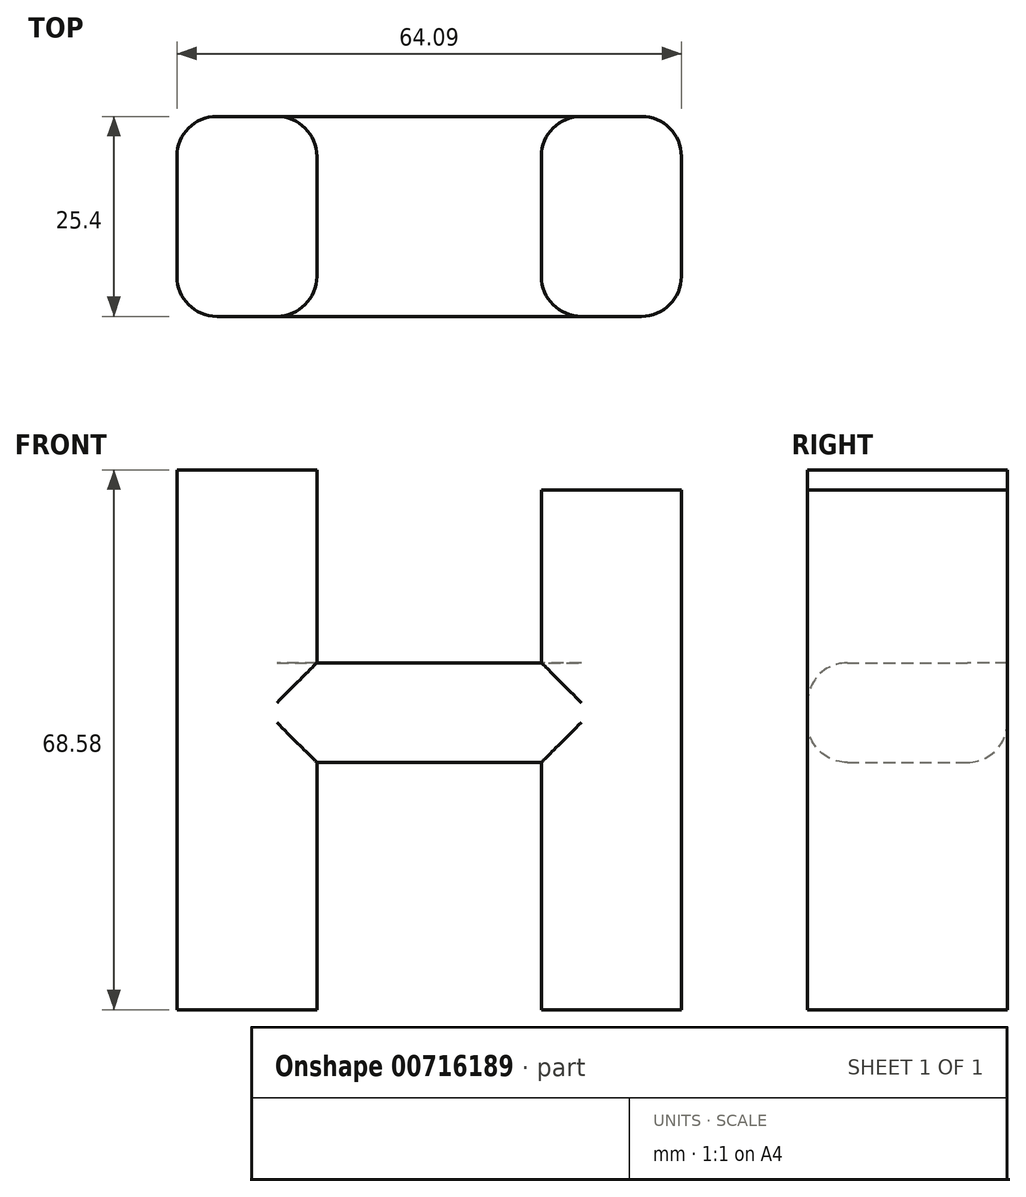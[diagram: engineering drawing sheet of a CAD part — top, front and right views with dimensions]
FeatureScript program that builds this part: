
annotation { "Feature Type Name" : "Feature", "Feature Type Description" : "" }
export const myFeature = defineFeature(function(context is Context, id is Id, definition is map)
    precondition{}
    {
        {
            var Q0;
            Q0=qCreatedBy(makeId("Front.planeOp"),FACE);
            var sketch = newSketch(context, id + "F0", { "sketchPlane" : qUnion([Q0])});
            skLineSegment(sketch, "E0.bottom", {"start": v(-8.9, 33.02) * mm, "end": v(8.9, 33.02) * mm});
            skLineSegment(sketch, "E0.top", {"start": v(-8.9, -33.02) * mm, "end": v(8.9, -33.02) * mm});
            skLineSegment(sketch, "E0.left", {"start": v(-8.9, 33.02) * mm, "end": v(-8.9, -33.02) * mm});
            skLineSegment(sketch, "E0.right", {"start": v(8.9, 33.02) * mm, "end": v(8.9, -33.02) * mm});
            skPoint(sketch, "E0.middle", {"position": v(0, 0) * mm});
            skLineSegment(sketch, "E1.bottom", {"start": v(37.42, 30.48) * mm, "end": v(55.2, 30.48) * mm});
            skLineSegment(sketch, "E1.top", {"start": v(37.42, -35.56) * mm, "end": v(55.2, -35.56) * mm});
            skLineSegment(sketch, "E1.left", {"start": v(37.42, 30.48) * mm, "end": v(37.42, -35.56) * mm});
            skLineSegment(sketch, "E1.right", {"start": v(55.2, 30.48) * mm, "end": v(55.2, -35.56) * mm});
            skLineSegment(sketch, "E2.bottom", {"start": v(8.9, 8.5) * mm, "end": v(37.42, 8.5) * mm});
            skLineSegment(sketch, "E2.top", {"start": v(8.9, -4.15) * mm, "end": v(37.42, -4.15) * mm});
            skLineSegment(sketch, "E2.left", {"start": v(8.9, 8.5) * mm, "end": v(8.9, -4.15) * mm});
            skLineSegment(sketch, "E2.right", {"start": v(37.42, 8.5) * mm, "end": v(37.42, -4.15) * mm});
            skLineSegment(sketch, "E3.top", {"start": v(-8.9, -35.56) * mm, "end": v(8.9, -35.56) * mm});
            skLineSegment(sketch, "E3.left", {"start": v(-8.9, -33.02) * mm, "end": v(-8.9, -35.56) * mm});
            skLineSegment(sketch, "E3.right", {"start": v(8.9, -33.02) * mm, "end": v(8.9, -35.56) * mm});
            skLineSegment(sketch, "E4.top", {"start": v(37.42, -31.16) * mm, "end": v(55.2, -31.16) * mm});
            skLineSegment(sketch, "E4.left", {"start": v(37.42, -31.16) * mm, "end": v(37.42, -35.56) * mm});
            skLineSegment(sketch, "E4.right", {"start": v(55.2, -31.16) * mm, "end": v(55.2, -35.56) * mm});
            skSolve(sketch);
        }
        {
            var Q0;
            {var subQ3=sQuery(id+"F0.wireOp",EDGE,"E0.bottom");Q0=makeQuery(id+"F0.imprint","IMPRINT",FACE,{"disambiguationData":[TD([[makeQuery(id+"F0.imprint","IMPRINT",EDGE,{"derivedFrom":subQ3}),-1.0]])]});}
            extrude(context, id + "F1", {"entities" : qUnion([Q0]), "depth" : 12.7 * mm, "offsetDistance" : 25.4 * mm});
        }
        {
            var Q0;
            Q0 = qSketchRegion(id + "F0", true);
            extrude(context, id + "F2", {"entities" : qUnion([Q0]), "operationType" : NewBodyOperationType.ADD, "depth" : 25.4 * mm, "offsetDistance" : 25.4 * mm});
        }
        {
            var Q0;
            Q0=makeQuery(id+"F2.opExtrude","CAP_EDGE",EDGE,{"disambiguationData":[OSD([sQuery(id+"F0.wireOp",EDGE,"E1.right"),sQuery(id+"F0.wireOp",EDGE,"E4.right")])],"isStart":false});
            var Q1;
            Q1=makeQuery(id+"F2.opExtrude","CAP_EDGE",EDGE,{"disambiguationData":[OSD([sQuery(id+"F0.wireOp",EDGE,"E1.right"),sQuery(id+"F0.wireOp",EDGE,"E4.right")])],"isStart":true});
            var Q2;
            Q2=makeQuery(id+"F2.opExtrude","CAP_EDGE",EDGE,{"disambiguationData":[OSD([sQuery(id+"F0.wireOp",EDGE,"E1.left")])],"isStart":false});
            var Q3;
            Q3=makeQuery(id+"F2.opExtrude","CAP_EDGE",EDGE,{"disambiguationData":[OSD([sQuery(id+"F0.wireOp",EDGE,"E0.right")])],"isStart":false});
            var Q4;
            Q4=makeQuery(id+"F2.opExtrude","CAP_EDGE",EDGE,{"disambiguationData":[OSD([sQuery(id+"F0.wireOp",EDGE,"E0.right"),sQuery(id+"F0.wireOp",EDGE,"E3.right")])],"isStart":false});
            var Q5;
            Q5=makeQuery(id+"F2.opExtrude","CAP_EDGE",EDGE,{"disambiguationData":[OSD([sQuery(id+"F0.wireOp",EDGE,"E0.left"),sQuery(id+"F0.wireOp",EDGE,"E3.left")])],"isStart":false});
            var Q6;
            Q6=makeQuery(id+"F2.opExtrude","CAP_EDGE",EDGE,{"disambiguationData":[OSD([sQuery(id+"F0.wireOp",EDGE,"E2.bottom")])],"isStart":false});
            var Q7;
            Q7=makeQuery(id+"F2.opExtrude","CAP_EDGE",EDGE,{"disambiguationData":[OSD([sQuery(id+"F0.wireOp",EDGE,"E2.top")])],"isStart":false});
            var Q8;
            Q8=makeQuery(id+"F2.opExtrude","CAP_EDGE",EDGE,{"disambiguationData":[OSD([sQuery(id+"F0.wireOp",EDGE,"E1.left")])],"isStart":true});
            var Q9;
            Q9=makeQuery(id+"F2.opExtrude","CAP_EDGE",EDGE,{"disambiguationData":[OSD([sQuery(id+"F0.wireOp",EDGE,"E1.left"),sQuery(id+"F0.wireOp",EDGE,"E4.left")])],"isStart":true});
            var Q10;
            Q10=makeQuery(id+"F2.opExtrude","CAP_EDGE",EDGE,{"disambiguationData":[OSD([sQuery(id+"F0.wireOp",EDGE,"E2.top")])],"isStart":true});
            var Q11;
            {var subQ0=sQuery(id+"F0.wireOp",EDGE,"E0.right");Q11=makeQuery(id+"F2.boolean.opBoolean","MERGE",EDGE,{"derivedFrom":[makeQuery(id+"F1.opExtrude","CAP_EDGE",EDGE,{"disambiguationData":[OSD([subQ0,sQuery(id+"F0.wireOp",EDGE,"E2.left")])],"isStart":true}),makeQuery(id+"F2.opExtrude","CAP_EDGE",EDGE,{"disambiguationData":[OSD([subQ0,sQuery(id+"F0.wireOp",EDGE,"E3.right")])],"isStart":true})]});}
            var Q12;
            Q12=makeQuery(id+"F2.boolean.opBoolean","SPLIT",EDGE,{"derivedFrom":makeQuery(id+"F1.opExtrude","CAP_EDGE",EDGE,{"disambiguationData":[OSD([sQuery(id+"F0.wireOp",EDGE,"E0.right"),sQuery(id+"F0.wireOp",EDGE,"E2.left")])],"isStart":true})});
            var Q13;
            {var subQ0=sQuery(id+"F0.wireOp",EDGE,"E0.left");Q13=makeQuery(id+"F2.boolean.opBoolean","MERGE",EDGE,{"derivedFrom":[makeQuery(id+"F1.opExtrude","CAP_EDGE",EDGE,{"disambiguationData":[OSD([subQ0])],"isStart":true}),makeQuery(id+"F2.opExtrude","CAP_EDGE",EDGE,{"disambiguationData":[OSD([subQ0,sQuery(id+"F0.wireOp",EDGE,"E3.left")])],"isStart":true})]});}
            fillet(context, id + "F3", {"entities" : qUnion([Q0, Q1, Q2, Q3, Q4, Q5, Q6, Q7, Q8, Q9, Q10, Q11, Q12, Q13]), "radius" : 5.08 * mm, "tangentPropagation" : true, "allowEdgeOverflow" : false});
        }
    });
